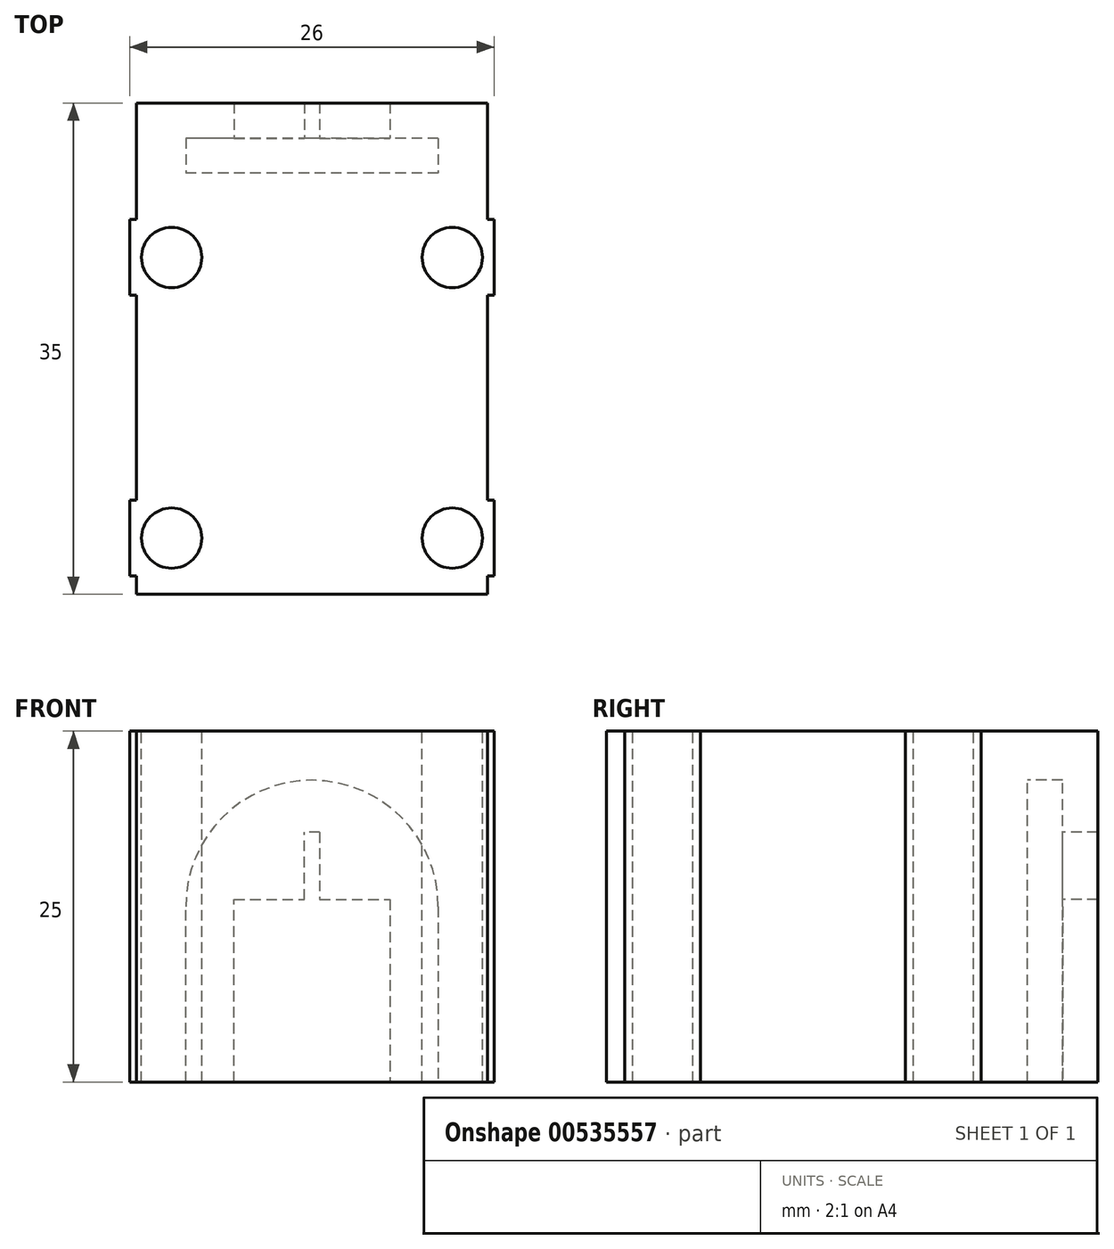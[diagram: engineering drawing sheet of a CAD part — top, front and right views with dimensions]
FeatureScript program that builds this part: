
annotation { "Feature Type Name" : "Feature", "Feature Type Description" : "" }
export const myFeature = defineFeature(function(context is Context, id is Id, definition is map)
    precondition{}
    {
        {
            var Q0;
            Q0=qCreatedBy(makeId("Front.planeOp"),FACE);
            var sketch = newSketch(context, id + "F0", { "sketchPlane" : qUnion([Q0])});
            skLineSegment(sketch, "E0.bottom", {"start": v(-12.5, 12.5) * mm, "end": v(12.5, 12.5) * mm});
            skLineSegment(sketch, "E0.top", {"start": v(-12.5, -12.5) * mm, "end": v(12.5, -12.5) * mm});
            skLineSegment(sketch, "E0.left", {"start": v(-12.5, 12.5) * mm, "end": v(-12.5, -12.5) * mm});
            skLineSegment(sketch, "E0.right", {"start": v(12.5, 12.5) * mm, "end": v(12.5, -12.5) * mm});
            skPoint(sketch, "E0.middle", {"position": v(0, 0) * mm});
            skSolve(sketch);
        }
        {
            var Q0;
            Q0 = qSketchRegion(id + "F0", true);
            extrude(context, id + "F1", {"entities" : qUnion([Q0]), "depth" : 30 * mm, "offsetDistance" : 25 * mm});
        }
        {
            var Q0;
            Q0=qCreatedBy(makeId("Front.planeOp"),FACE);
            var sketch = newSketch(context, id + "F2", { "sketchPlane" : qUnion([Q0])});
            skLineSegment(sketch, "E1.bottom", {"start": v(12.5, 12.5) * mm, "end": v(-12.5, 12.5) * mm});
            skLineSegment(sketch, "E1.top", {"start": v(12.5, -12.5) * mm, "end": v(-12.5, -12.5) * mm});
            skLineSegment(sketch, "E1.left", {"start": v(12.5, 12.5) * mm, "end": v(12.5, -12.5) * mm});
            skLineSegment(sketch, "E1.right", {"start": v(-12.5, 12.5) * mm, "end": v(-12.5, -12.5) * mm});
            skPoint(sketch, "E1.middle", {"position": v(0, 0) * mm});
            skSolve(sketch);
        }
        {
            var Q0;
            Q0 = qSketchRegion(id + "F2", true);
            extrude(context, id + "F3", {"entities" : qUnion([Q0]), "operationType" : NewBodyOperationType.ADD, "oppositeDirection" : true, "depth" : 5 * mm, "offsetDistance" : 25 * mm});
        }
        {
            var Q0;
            Q0=qCreatedBy(makeId("Front.planeOp"),FACE);
            var sketch = newSketch(context, id + "F4", { "sketchPlane" : qUnion([Q0])});
            skCircle(sketch, "E2", {"center": v(0, 0) * mm, "radius": 9 * mm});
            skLineSegment(sketch, "E3", {"start": v(9, 0) * mm, "end": v(9, -12.5) * mm});
            skLineSegment(sketch, "E4", {"start": v(9, -12.5) * mm, "end": v(-9, -12.5) * mm});
            skLineSegment(sketch, "E5", {"start": v(-9, -12.5) * mm, "end": v(-9, 0) * mm});
            skSolve(sketch);
        }
        {
            var Q0;
            Q0 = qSketchRegion(id + "F4", true);
            extrude(context, id + "F5", {"entities" : qUnion([Q0]), "operationType" : NewBodyOperationType.REMOVE, "oppositeDirection" : true, "depth" : 2.5 * mm, "offsetDistance" : 25 * mm});
        }
        {
            var Q0;
            Q0=qCreatedBy(makeId("Front.planeOp"),FACE);
            var sketch = newSketch(context, id + "F6", { "sketchPlane" : qUnion([Q0])});
            skLineSegment(sketch, "E6", {"start": v(0.55, 5.3) * mm, "end": v(-0.55, 5.3) * mm});
            skLineSegment(sketch, "E7", {"start": v(0.55, 5.3) * mm, "end": v(0.55, 0.5) * mm});
            skLineSegment(sketch, "E8", {"start": v(0.55, 0.5) * mm, "end": v(5.55, 0.5) * mm});
            skLineSegment(sketch, "E9", {"start": v(5.55, 0.5) * mm, "end": v(5.55, -12.5) * mm});
            skLineSegment(sketch, "E10", {"start": v(5.55, -12.5) * mm, "end": v(-5.55, -12.5) * mm});
            skLineSegment(sketch, "E11", {"start": v(-5.55, -12.5) * mm, "end": v(-5.55, 0.5) * mm});
            skLineSegment(sketch, "E12", {"start": v(-5.55, 0.5) * mm, "end": v(-0.55, 0.5) * mm});
            skLineSegment(sketch, "E13", {"start": v(-0.55, 0.5) * mm, "end": v(-0.55, 5.3) * mm});
            skSolve(sketch);
        }
        {
            var Q0;
            Q0 = qSketchRegion(id + "F6", true);
            extrude(context, id + "F7", {"entities" : qUnion([Q0]), "operationType" : NewBodyOperationType.REMOVE, "oppositeDirection" : true, "depth" : 25 * mm, "offsetDistance" : 25 * mm});
        }
        {
            var Q0;
            Q0=qCreatedBy(makeId("Top.planeOp"),FACE);
            var sketch = newSketch(context, id + "F8", { "sketchPlane" : qUnion([Q0])});
            skCircle(sketch, "E14", {"center": v(-10, -6) * mm, "radius": 2.15 * mm});
            skCircle(sketch, "E15", {"center": v(-10, -26) * mm, "radius": 2.15 * mm});
            skCircle(sketch, "E16.MirrorC", {"center": v(10, -6) * mm, "radius": 2.15 * mm});
            skCircle(sketch, "E17.MirrorC", {"center": v(10, -26) * mm, "radius": 2.15 * mm});
            skSolve(sketch);
        }
        {
            var Q0;
            Q0=qCreatedBy(makeId("Top.planeOp"),FACE);
            var sketch = newSketch(context, id + "F9", { "sketchPlane" : qUnion([Q0])});
            skLineSegment(sketch, "E18.bottom", {"start": v(0, -3.3) * mm, "end": v(-13, -3.3) * mm});
            skLineSegment(sketch, "E18.top", {"start": v(0, -8.7) * mm, "end": v(-13, -8.7) * mm});
            skLineSegment(sketch, "E18.left", {"start": v(0, -3.3) * mm, "end": v(0, -8.7) * mm});
            skLineSegment(sketch, "E18.right", {"start": v(-13, -3.3) * mm, "end": v(-13, -8.7) * mm});
            skLineSegment(sketch, "E19.bottom", {"start": v(0, -23.3) * mm, "end": v(-13, -23.3) * mm});
            skLineSegment(sketch, "E19.top", {"start": v(0, -28.7) * mm, "end": v(-13, -28.7) * mm});
            skLineSegment(sketch, "E19.left", {"start": v(0, -23.3) * mm, "end": v(0, -28.7) * mm});
            skLineSegment(sketch, "E19.right", {"start": v(-13, -23.3) * mm, "end": v(-13, -28.7) * mm});
            skLineSegment(sketch, "E20.MirrorCS", {"start": v(0, -3.3) * mm, "end": v(13, -3.3) * mm});
            skLineSegment(sketch, "E21.MirrorCS", {"start": v(0, -8.7) * mm, "end": v(13, -8.7) * mm});
            skLineSegment(sketch, "E22.MirrorCS", {"start": v(13, -3.3) * mm, "end": v(13, -8.7) * mm});
            skLineSegment(sketch, "E23.MirrorCS", {"start": v(0, -23.3) * mm, "end": v(13, -23.3) * mm});
            skLineSegment(sketch, "E24.MirrorCS", {"start": v(13, -23.3) * mm, "end": v(13, -28.7) * mm});
            skLineSegment(sketch, "E25.MirrorCS", {"start": v(0, -28.7) * mm, "end": v(13, -28.7) * mm});
            skSolve(sketch);
        }
        {
            var Q0;
            Q0 = qSketchRegion(id + "F9", true);
            extrude(context, id + "F10", {"entities" : qUnion([Q0]), "operationType" : NewBodyOperationType.ADD, "depth" : 25 * mm, "offsetDistance" : 25 * mm, "symmetric" : true});
        }
        {
            var Q0;
            Q0 = qSketchRegion(id + "F8", true);
            extrude(context, id + "F11", {"entities" : qUnion([Q0]), "operationType" : NewBodyOperationType.REMOVE, "oppositeDirection" : true, "depth" : 25 * mm, "offsetDistance" : 25 * mm, "symmetric" : true});
        }
    });
